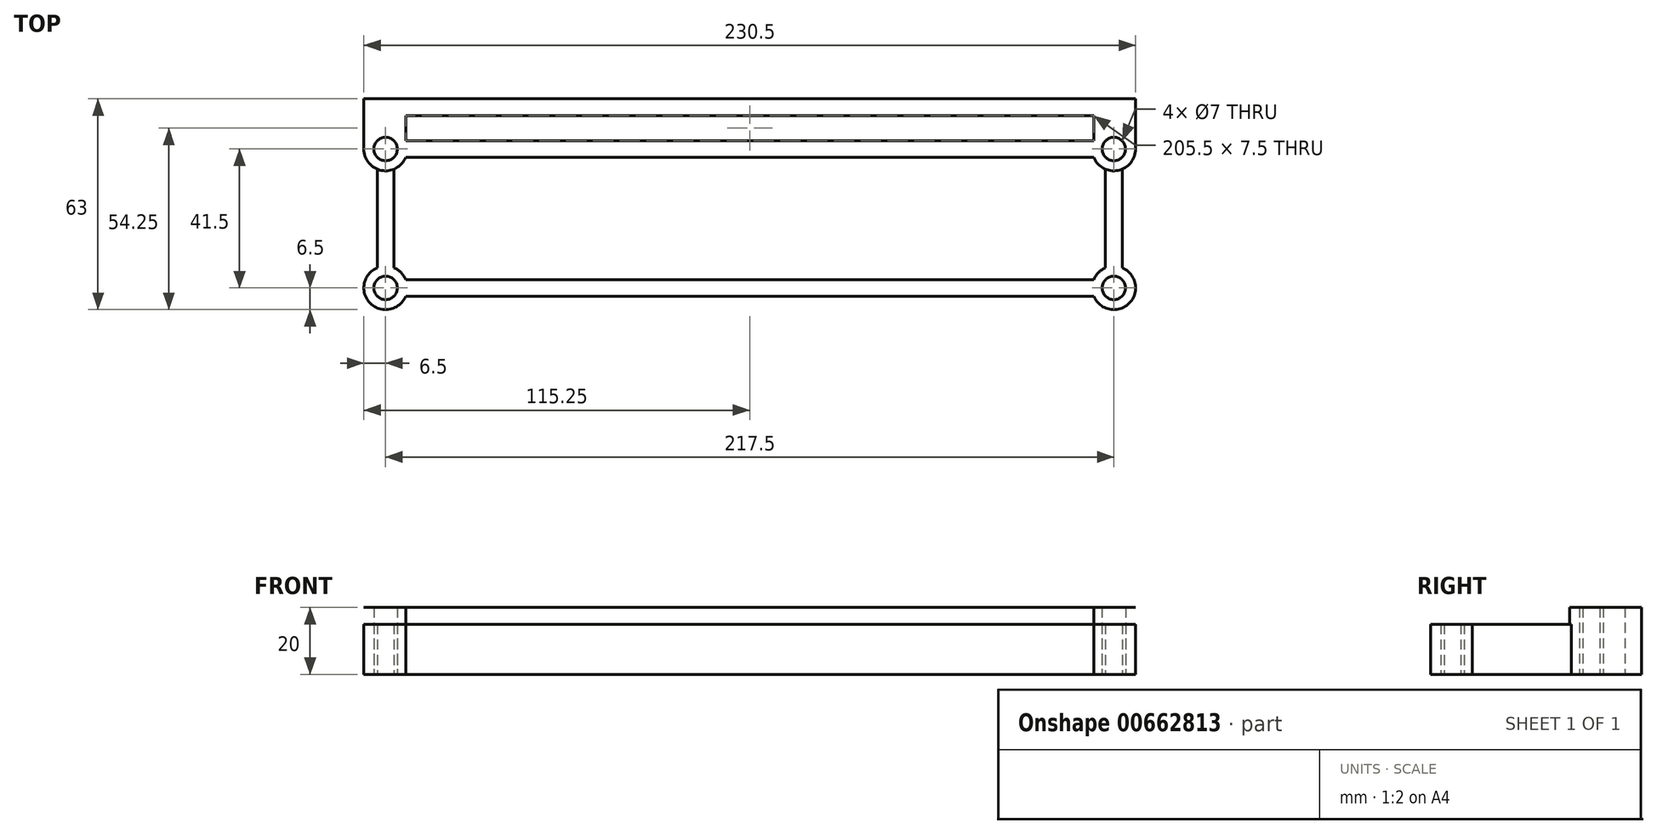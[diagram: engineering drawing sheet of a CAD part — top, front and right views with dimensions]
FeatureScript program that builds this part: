
annotation { "Feature Type Name" : "Feature", "Feature Type Description" : "" }
export const myFeature = defineFeature(function(context is Context, id is Id, definition is map)
    precondition{}
    {
        {
            var Q0;
            Q0=qCreatedBy(makeId("Top.planeOp"),FACE);
            var sketch = newSketch(context, id + "F0", { "sketchPlane" : qUnion([Q0])});
            skCircle(sketch, "E0", {"center": v(-108.75, 28.07) * mm, "radius": 3.5 * mm});
            skArc(sketch, "E1", {"start": v(-115.25, 28.07) * mm, "mid": v(-114.16, 24.46) * mm, "end": v(-111.25, 22.07) * mm});
            skCircle(sketch, "E2", {"center": v(108.75, 28.07) * mm, "radius": 3.5 * mm});
            skArc(sketch, "E3", {"start": v(102.75, 25.57) * mm, "mid": v(104.15, 23.47) * mm, "end": v(106.25, 22.07) * mm});
            skLineSegment(sketch, "E4.bottom", {"start": v(-102.75, 30.57) * mm, "end": v(102.75, 30.57) * mm});
            skLineSegment(sketch, "E4.top", {"start": v(-102.75, 25.57) * mm, "end": v(102.75, 25.57) * mm});
            skLineSegment(sketch, "E5", {"start": v(-108.75, 28.07) * mm, "end": v(-122.06, 28.07) * mm, "construction": true});
            skCircle(sketch, "E6", {"center": v(-108.75, -13.43) * mm, "radius": 3.5 * mm});
            skArc(sketch, "E7", {"start": v(-102.75, -10.93) * mm, "mid": v(-104.15, -8.83) * mm, "end": v(-106.25, -7.43) * mm});
            skCircle(sketch, "E8", {"center": v(108.75, -13.43) * mm, "radius": 3.5 * mm});
            skArc(sketch, "E9", {"start": v(102.75, -15.93) * mm, "mid": v(113.35, -18.03) * mm, "end": v(111.25, -7.43) * mm});
            skLineSegment(sketch, "E10.left", {"start": v(-111.25, 22.07) * mm, "end": v(-111.25, -7.43) * mm});
            skLineSegment(sketch, "E10.right", {"start": v(-106.25, 22.07) * mm, "end": v(-106.25, -7.43) * mm});
            skLineSegment(sketch, "E11.bottom", {"start": v(-102.75, -10.93) * mm, "end": v(102.75, -10.93) * mm});
            skLineSegment(sketch, "E11.top", {"start": v(-102.75, -15.93) * mm, "end": v(102.75, -15.93) * mm});
            skLineSegment(sketch, "E12.left", {"start": v(106.25, 22.07) * mm, "end": v(106.25, -7.43) * mm});
            skLineSegment(sketch, "E12.right", {"start": v(111.25, 22.07) * mm, "end": v(111.25, -7.43) * mm});
            skArc(sketch, "E13.trimOffspring", {"start": v(-111.25, -7.43) * mm, "mid": v(-113.35, -18.03) * mm, "end": v(-102.75, -15.93) * mm});
            skArc(sketch, "E14.trimOffspring", {"start": v(-106.25, 22.07) * mm, "mid": v(-104.15, 23.47) * mm, "end": v(-102.75, 25.57) * mm});
            skArc(sketch, "E15.trimOffspring", {"start": v(106.25, -7.43) * mm, "mid": v(104.15, -8.83) * mm, "end": v(102.75, -10.93) * mm});
            skArc(sketch, "E16.trimOffspring", {"start": v(111.25, 22.07) * mm, "mid": v(114.16, 24.46) * mm, "end": v(115.25, 28.07) * mm});
            skLineSegment(sketch, "E17", {"start": v(-115.25, 43.07) * mm, "end": v(115.25, 43.07) * mm});
            skLineSegment(sketch, "E18", {"start": v(-115.25, 28.07) * mm, "end": v(-115.25, 43.07) * mm});
            skPoint(sketch, "E19.orphan", {"position": v(-110.78, 43.07) * mm});
            skLineSegment(sketch, "E20", {"start": v(115.25, 28.07) * mm, "end": v(115.25, 43.07) * mm});
            skLineSegment(sketch, "E21", {"start": v(102.75, 30.57) * mm, "end": v(102.75, 38.07) * mm});
            skLineSegment(sketch, "E22.0", {"start": v(-102.75, 38.07) * mm, "end": v(102.75, 38.07) * mm});
            skLineSegment(sketch, "E23", {"start": v(-102.75, 30.57) * mm, "end": v(-102.75, 38.07) * mm});
            skSolve(sketch);
        }
        {
            var Q0;
            Q0 = qSketchRegion(id + "F0", true);
            extrude(context, id + "F1", {"entities" : qUnion([Q0]), "depth" : 7 * mm, "offsetDistance" : 25 * mm});
        }
        {
            var Q0;
            Q0=makeQuery(id+"F1.opExtrude","CAP_FACE",FACE,{"disambiguationData":[OSD([sQuery(id+"F0.wireOp",EDGE,"E0"),sQuery(id+"F0.wireOp",EDGE,"E1"),sQuery(id+"F0.wireOp",EDGE,"E2"),sQuery(id+"F0.wireOp",EDGE,"E3"),sQuery(id+"F0.wireOp",EDGE,"E4.bottom"),sQuery(id+"F0.wireOp",EDGE,"E4.top"),sQuery(id+"F0.wireOp",EDGE,"E6"),sQuery(id+"F0.wireOp",EDGE,"E7"),sQuery(id+"F0.wireOp",EDGE,"E8"),sQuery(id+"F0.wireOp",EDGE,"E9"),sQuery(id+"F0.wireOp",EDGE,"E10.left"),sQuery(id+"F0.wireOp",EDGE,"E10.right"),sQuery(id+"F0.wireOp",EDGE,"E11.bottom"),sQuery(id+"F0.wireOp",EDGE,"E11.top"),sQuery(id+"F0.wireOp",EDGE,"E12.left"),sQuery(id+"F0.wireOp",EDGE,"E12.right"),sQuery(id+"F0.wireOp",EDGE,"E13.trimOffspring"),sQuery(id+"F0.wireOp",EDGE,"E14.trimOffspring"),sQuery(id+"F0.wireOp",EDGE,"E15.trimOffspring"),sQuery(id+"F0.wireOp",EDGE,"E16.trimOffspring"),sQuery(id+"F0.wireOp",EDGE,"E17"),sQuery(id+"F0.wireOp",EDGE,"E18"),sQuery(id+"F0.wireOp",EDGE,"E20"),sQuery(id+"F0.wireOp",EDGE,"E21"),sQuery(id+"F0.wireOp",EDGE,"E22.0"),sQuery(id+"F0.wireOp",EDGE,"E23")])],"isStart":false});
            var sketch = newSketch(context, id + "F2", { "sketchPlane" : qUnion([Q0])});
            skLineSegment(sketch, "E24.0", {"start": v(-115.25, 43.07) * mm, "end": v(115.25, 43.07) * mm});
            skLineSegment(sketch, "E25.0", {"start": v(-115.25, 28.07) * mm, "end": v(-115.25, 43.07) * mm});
            skLineSegment(sketch, "E26.0", {"start": v(-102.75, 30.57) * mm, "end": v(-102.75, 38.07) * mm});
            skLineSegment(sketch, "E27.0", {"start": v(-102.75, 30.57) * mm, "end": v(102.75, 30.57) * mm});
            skLineSegment(sketch, "E28.0", {"start": v(-102.75, 38.07) * mm, "end": v(102.75, 38.07) * mm});
            skPoint(sketch, "E29.0", {"position": v(102.75, 34.32) * mm});
            skCircle(sketch, "E30.0", {"center": v(108.75, 28.07) * mm, "radius": 3.5 * mm});
            skLineSegment(sketch, "E31.0", {"start": v(115.25, 28.07) * mm, "end": v(115.25, 43.07) * mm});
            skCircle(sketch, "E32.0", {"center": v(-108.75, 28.07) * mm, "radius": 3.5 * mm});
            skArc(sketch, "E33.0", {"start": v(-115.25, 28.07) * mm, "mid": v(-114.16, 24.46) * mm, "end": v(-111.25, 22.07) * mm});
            skArc(sketch, "E34.0", {"start": v(-106.25, 22.07) * mm, "mid": v(-104.15, 23.47) * mm, "end": v(-102.75, 25.57) * mm});
            skLineSegment(sketch, "E35.0", {"start": v(-102.75, 25.57) * mm, "end": v(102.75, 25.57) * mm});
            skArc(sketch, "E36.0", {"start": v(102.75, 25.57) * mm, "mid": v(104.15, 23.47) * mm, "end": v(106.25, 22.07) * mm});
            skArc(sketch, "E37.0", {"start": v(111.25, 22.07) * mm, "mid": v(114.16, 24.46) * mm, "end": v(115.25, 28.07) * mm});
            skArc(sketch, "E38", {"start": v(106.25, 22.07) * mm, "mid": v(108.75, 21.57) * mm, "end": v(111.25, 22.07) * mm});
            skArc(sketch, "E39", {"start": v(-111.25, 22.07) * mm, "mid": v(-108.75, 21.57) * mm, "end": v(-106.25, 22.07) * mm});
            skLineSegment(sketch, "E40", {"start": v(102.75, 30.57) * mm, "end": v(102.75, 38.07) * mm});
            skSolve(sketch);
        }
        {
            var Q0;
            Q0 = qSketchRegion(id + "F2", true);
            extrude(context, id + "F3", {"entities" : qUnion([Q0]), "operationType" : NewBodyOperationType.ADD, "depth" : 5 * mm, "offsetDistance" : 25 * mm});
        }
        {
            var Q0;
            Q0=makeQuery(id+"F1.opExtrude","CAP_FACE",FACE,{"disambiguationData":[OSD([sQuery(id+"F0.wireOp",EDGE,"E0"),sQuery(id+"F0.wireOp",EDGE,"E1"),sQuery(id+"F0.wireOp",EDGE,"E2"),sQuery(id+"F0.wireOp",EDGE,"E3"),sQuery(id+"F0.wireOp",EDGE,"E4.bottom"),sQuery(id+"F0.wireOp",EDGE,"E4.top"),sQuery(id+"F0.wireOp",EDGE,"E6"),sQuery(id+"F0.wireOp",EDGE,"E7"),sQuery(id+"F0.wireOp",EDGE,"E8"),sQuery(id+"F0.wireOp",EDGE,"E9"),sQuery(id+"F0.wireOp",EDGE,"E10.left"),sQuery(id+"F0.wireOp",EDGE,"E10.right"),sQuery(id+"F0.wireOp",EDGE,"E11.bottom"),sQuery(id+"F0.wireOp",EDGE,"E11.top"),sQuery(id+"F0.wireOp",EDGE,"E12.left"),sQuery(id+"F0.wireOp",EDGE,"E12.right"),sQuery(id+"F0.wireOp",EDGE,"E13.trimOffspring"),sQuery(id+"F0.wireOp",EDGE,"E14.trimOffspring"),sQuery(id+"F0.wireOp",EDGE,"E15.trimOffspring"),sQuery(id+"F0.wireOp",EDGE,"E16.trimOffspring"),sQuery(id+"F0.wireOp",EDGE,"E17"),sQuery(id+"F0.wireOp",EDGE,"E18"),sQuery(id+"F0.wireOp",EDGE,"E20"),sQuery(id+"F0.wireOp",EDGE,"E21"),sQuery(id+"F0.wireOp",EDGE,"E22.0"),sQuery(id+"F0.wireOp",EDGE,"E23")])],"isStart":true});
            var sketch = newSketch(context, id + "F4", { "sketchPlane" : qUnion([Q0])});
            skLineSegment(sketch, "E41.0.0", {"start": v(111.25, -22.07) * mm, "end": v(111.25, 7.43) * mm});
            skArc(sketch, "E41.0.1", {"start": v(111.25, 7.43) * mm, "mid": v(113.35, 18.03) * mm, "end": v(102.75, 15.93) * mm});
            skLineSegment(sketch, "E41.0.2", {"start": v(102.75, 15.93) * mm, "end": v(-102.75, 15.93) * mm});
            skArc(sketch, "E41.0.3", {"start": v(-102.75, 15.93) * mm, "mid": v(-113.35, 18.03) * mm, "end": v(-111.25, 7.43) * mm});
            skLineSegment(sketch, "E41.0.4", {"start": v(-111.25, 7.43) * mm, "end": v(-111.25, -22.07) * mm});
            skArc(sketch, "E41.0.5", {"start": v(-111.25, -22.07) * mm, "mid": v(-114.16, -24.46) * mm, "end": v(-115.25, -28.07) * mm});
            skLineSegment(sketch, "E41.0.6", {"start": v(-115.25, -28.07) * mm, "end": v(-115.25, -43.07) * mm});
            skLineSegment(sketch, "E41.0.7", {"start": v(-115.25, -43.07) * mm, "end": v(115.25, -43.07) * mm});
            skLineSegment(sketch, "E41.0.8", {"start": v(115.25, -43.07) * mm, "end": v(115.25, -28.07) * mm});
            skArc(sketch, "E41.0.9", {"start": v(115.25, -28.07) * mm, "mid": v(114.16, -24.46) * mm, "end": v(111.25, -22.07) * mm});
            skLineSegment(sketch, "E42.0", {"start": v(-102.75, -38.07) * mm, "end": v(102.75, -38.07) * mm});
            skLineSegment(sketch, "E43.0", {"start": v(102.75, -30.57) * mm, "end": v(102.75, -38.07) * mm});
            skLineSegment(sketch, "E44.0", {"start": v(-102.75, -30.57) * mm, "end": v(102.75, -30.57) * mm});
            skCircle(sketch, "E45.0", {"center": v(108.75, -28.07) * mm, "radius": 3.5 * mm});
            skCircle(sketch, "E46.0", {"center": v(108.75, 13.43) * mm, "radius": 3.5 * mm});
            skPoint(sketch, "E47.0", {"position": v(104.15, 8.83) * mm});
            skArc(sketch, "E48.0", {"start": v(106.25, 7.43) * mm, "mid": v(104.15, 8.83) * mm, "end": v(102.75, 10.93) * mm});
            skLineSegment(sketch, "E49.0", {"start": v(-102.75, 10.93) * mm, "end": v(102.75, 10.93) * mm});
            skLineSegment(sketch, "E50.0", {"start": v(-102.75, -25.57) * mm, "end": v(102.75, -25.57) * mm});
            skArc(sketch, "E51.0", {"start": v(102.75, -25.57) * mm, "mid": v(104.15, -23.47) * mm, "end": v(106.25, -22.07) * mm});
            skLineSegment(sketch, "E52.0", {"start": v(106.25, -22.07) * mm, "end": v(106.25, 7.43) * mm});
            skCircle(sketch, "E53.0", {"center": v(-108.75, -28.07) * mm, "radius": 3.5 * mm});
            skArc(sketch, "E54.0", {"start": v(-106.25, -22.07) * mm, "mid": v(-104.15, -23.47) * mm, "end": v(-102.75, -25.57) * mm});
            skLineSegment(sketch, "E55.0", {"start": v(-106.25, -22.07) * mm, "end": v(-106.25, 7.43) * mm});
            skArc(sketch, "E56.0", {"start": v(-102.75, 10.93) * mm, "mid": v(-104.15, 8.83) * mm, "end": v(-106.25, 7.43) * mm});
            skCircle(sketch, "E57.0", {"center": v(-108.75, 13.43) * mm, "radius": 3.5 * mm});
            skLineSegment(sketch, "E58.0", {"start": v(-102.75, -30.57) * mm, "end": v(-102.75, -38.07) * mm});
            skSolve(sketch);
        }
        {
            var Q0;
            Q0 = qSketchRegion(id + "F4", true);
            extrude(context, id + "F5", {"entities" : qUnion([Q0]), "operationType" : NewBodyOperationType.ADD, "depth" : 8 * mm, "offsetDistance" : 25 * mm});
        }
    });
